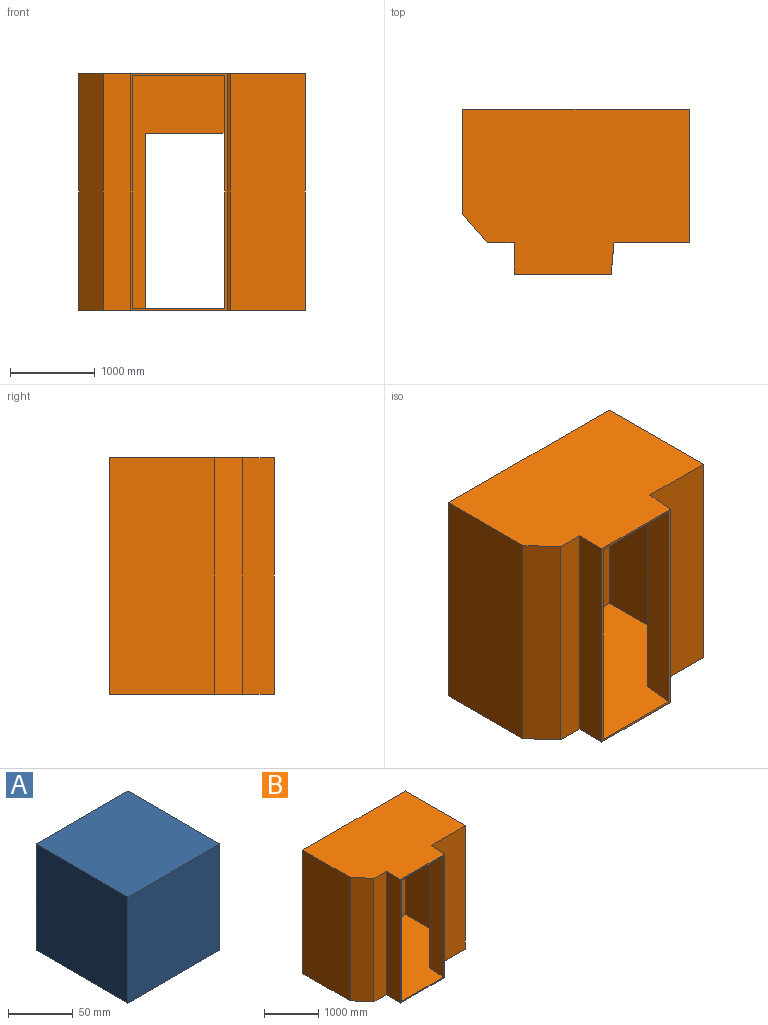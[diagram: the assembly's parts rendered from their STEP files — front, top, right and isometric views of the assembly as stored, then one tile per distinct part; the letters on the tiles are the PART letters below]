
ASSEMBLY  parts=2 mates=1
PART A: 6 faces, bbox 100x100x100 mm
  f0: plane 100x100mm, normal (1,0,0), area 10000mm2, adj f1,f3,f4,f5
  f1: plane 100x100mm, normal (0,1,0), area 10000mm2, adj f0,f2,f4,f5
  f2: plane 100x100mm, normal (-1,0,0), area 10000mm2, adj f1,f3,f4,f5
  f3: plane 100x100mm, normal (0,-1,0), area 10000mm2, adj f0,f2,f4,f5
  f4: plane 100x100mm, normal (0,0,1), area 10000mm2, adj f0,f1,f2,f3
  f5: plane 100x100mm, normal (0,0,-1), area 10000mm2, adj f0,f1,f2,f3
PART B: 24 faces, bbox 2670x1940x2785 mm
  f0: plane 2735x2620mm, normal (0,-1,0), area 4693700mm2, adj f16,f17,f19,f20,f21,f22,f23
  f1: plane 2785x1140.11mm, normal (0,-1,0), area 194050.4mm2, adj f3,f4,f10,f11,f13,f14,f19,f20
  f2: plane 2785x316.29mm, normal (0,-1,0), area 880854.9mm2, adj f3,f9,f10,f11
  f3: plane 2785x375mm, normal (-1,0,0), area 1044375mm2, adj f1,f2,f10,f11
  f4: plane 2785x375mm, normal (1,-0.09,0), area 1048880.7mm2, adj f1,f5,f10,f11
  f5: plane 2785x887.22mm, normal (0,-1,0), area 2470899.1mm2, adj f4,f6,f10,f11
  f6: plane 2785x1565mm, normal (1,0,0), area 4358525mm2, adj f5,f7,f10,f11
  f7: plane 2785x2670mm, normal (0,1,0), area 4963950mm2, adj f6,f8,f10,f11,f20,f21,f22,f23
  f8: plane 2785x1234.45mm, normal (-1,0,0), area 3437940.8mm2, adj f7,f9,f10,f11
  f9: plane 2785x330.55mm, normal (-0.75,-0.66,0), area 1227445.6mm2, adj f2,f8,f10,f11
  f10: plane 2670x1940mm, normal (0,0,1), area 4564448mm2, adj f1,f2,f3,f4,f5,f6,f7,f8
  f11: plane 2670x1940mm, normal (0,0,-1), area 4564448mm2, adj f1,f2,f3,f4,f5,f6,f7,f8
  f12: plane 2735x330mm, normal (0,1,0), area 902550mm2, adj f13,f18,f19,f20
  f13: plane 2735x400mm, normal (1,0,0), area 1094000mm2, adj f1,f12,f19,f20
  f14: plane 2735x400mm, normal (-1,0.09,0), area 1098719.8mm2, adj f1,f15,f19,f20
  f15: plane 2735x885mm, normal (0,1,0), area 2420475mm2, adj f14,f16,f19,f20
  f16: plane 2735x1515mm, normal (-1,0,0), area 4143525mm2, adj f0,f15,f19,f20
  f17: plane 2735x1200mm, normal (1,0,0), area 3282000mm2, adj f0,f18,f19,f20
  f18: plane 2735x315mm, normal (0.75,0.66,0), area 1148700mm2, adj f12,f17,f19,f20
  f19: plane 2620x1915mm, normal (0,0,-1), area 4368985.1mm2, adj f0,f1,f12,f13,f14,f15,f16,f17
  f20: plane 2620x1940mm, normal (0,0,1), area 4398985.1mm2, adj f0,f1,f7,f12,f13,f14,f15,f16
  f21: plane 2060x25mm, normal (-1,0,0), area 51500mm2, adj f0,f7,f20,f23
  f22: plane 2060x25mm, normal (1,0,0), area 51500mm2, adj f0,f7,f20,f23
  f23: plane 1200x25mm, normal (0,0,-1), area 30000mm2, adj f0,f7,f21,f22
PLACE A t=(-2520,1415,0)mm
PLACE B at identity fixed
MATE fastened A.f5 <-> B.f20  axis (0,0,1) through (-2620,1515,0)mm
